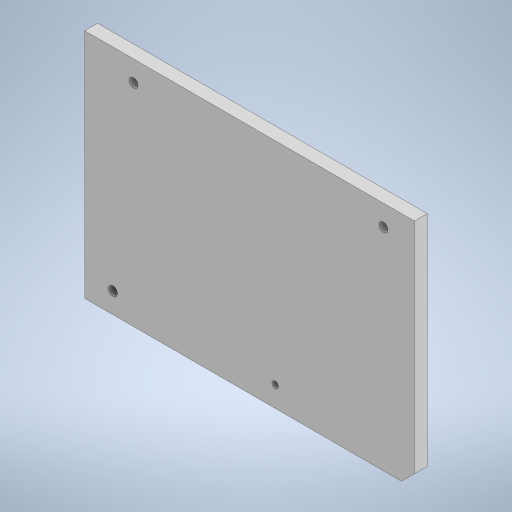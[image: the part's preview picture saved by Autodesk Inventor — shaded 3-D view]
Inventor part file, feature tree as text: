
AUTODESK INVENTOR PART (.ipt)
format: ipt  version: 2023 (Build 270158000, 158)  size: 207,360 bytes
history: native  units: mm
features: other x1, extrude x1, sketch x1
ambient origin geometry x8: Origin, YZ Plane, XZ Plane, XY Plane, X Axis, Y Axis, Z Axis, Center Point
bodies: Body1 (feature_tree)
feature tree (3):
  other  "솔리드1"
  extrude  "돌출1"  Depth=128.0mm
  sketch  "스케치1"
